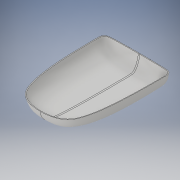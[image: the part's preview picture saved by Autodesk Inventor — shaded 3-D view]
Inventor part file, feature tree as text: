
AUTODESK INVENTOR PART (.ipt)
format: ipt  version: 2019.3 (Build 233278000, 278)  size: 6,051,328 bytes
history: native  units: mm
features: other x18, sketch x4, plane x3, surface_op x3, loft x2, extrude x2, shell x1, mirror x1
ambient origin geometry x8: Origin, YZ Plane, XZ Plane, XY Plane, X Axis, Y Axis, Z Axis, Center Point
bodies: Solid8 (feature_tree)
feature tree (34):
  other  "deck.ipt"
  sketch  "Sketch1"  dims[d15=212.0mm d47=28.0mm d48=145.0mm]
  sketch  "Sketch2"  dims[d107=200.0mm d108=10.0mm]
  sketch  "Sketch3"  dims[d122=84.0mm d130=110.0mm]
  other  "Transversal (front)"
  other  "Longitudinal"
  plane  "Work Plane9"
  other  "Transversal (mid)"
  plane  "Work Plane1"
  other  "Transversal (back)"
  plane  "Work Plane7"
  other  "Top"
  loft  "Loft4"
  shell  "Shell1"  Thickness=145.0mm
  extrude  "Extrusion1"  Depth=200.0mm
  mirror  "Mirror1"
  extrude  "Extrusion2"  Depth=110.0mm
  other  "Image2"
  other  "Image3"
  other  "Image4"
  other  "Front Profile"
  other  "Srf48"
  other  "Srf49"
  other  "Srf50"
  other  "Edges57"
  other  "Edges58"
  other  "Edges59"
  other  "Edges60"
  other  "Srf51"
  sketch  "Sketch20"  dims[d144=25.0mm d145=25.0mm d150=63.0mm d190=35.5mm d191=38.8mm d192=39.5mm d193=34.5mm d194=110.0mm d195=200.0mm d196=81.0mm d197=25.0mm d199=20.776473mm d316=3.0mm d321=3.0mm d423=140.0mm d425=205.0mm d429=141.0mm d430=250.0mm d455=57.0mm d460=57.0mm d461=0.0mm d462=90.0deg d463=0.0mm d464=90.0deg d465=0.0mm d466=90.0deg d467=0.0mm d468=90.0deg d472=0.0mm d473=90.0deg d474=0.0mm d475=90.0deg d476=0.0mm d477=90.0deg d478=0.0mm d479=90.0deg d480=1.9mm d481=10.0mm d482=0.0mm d483=0.0mm d484=0.0mm]
  loft  "LoftSrf13"
  surface_op  "Boundary Patch25"
  surface_op  "Boundary Patch26"
  surface_op  "Boundary Patch27"
